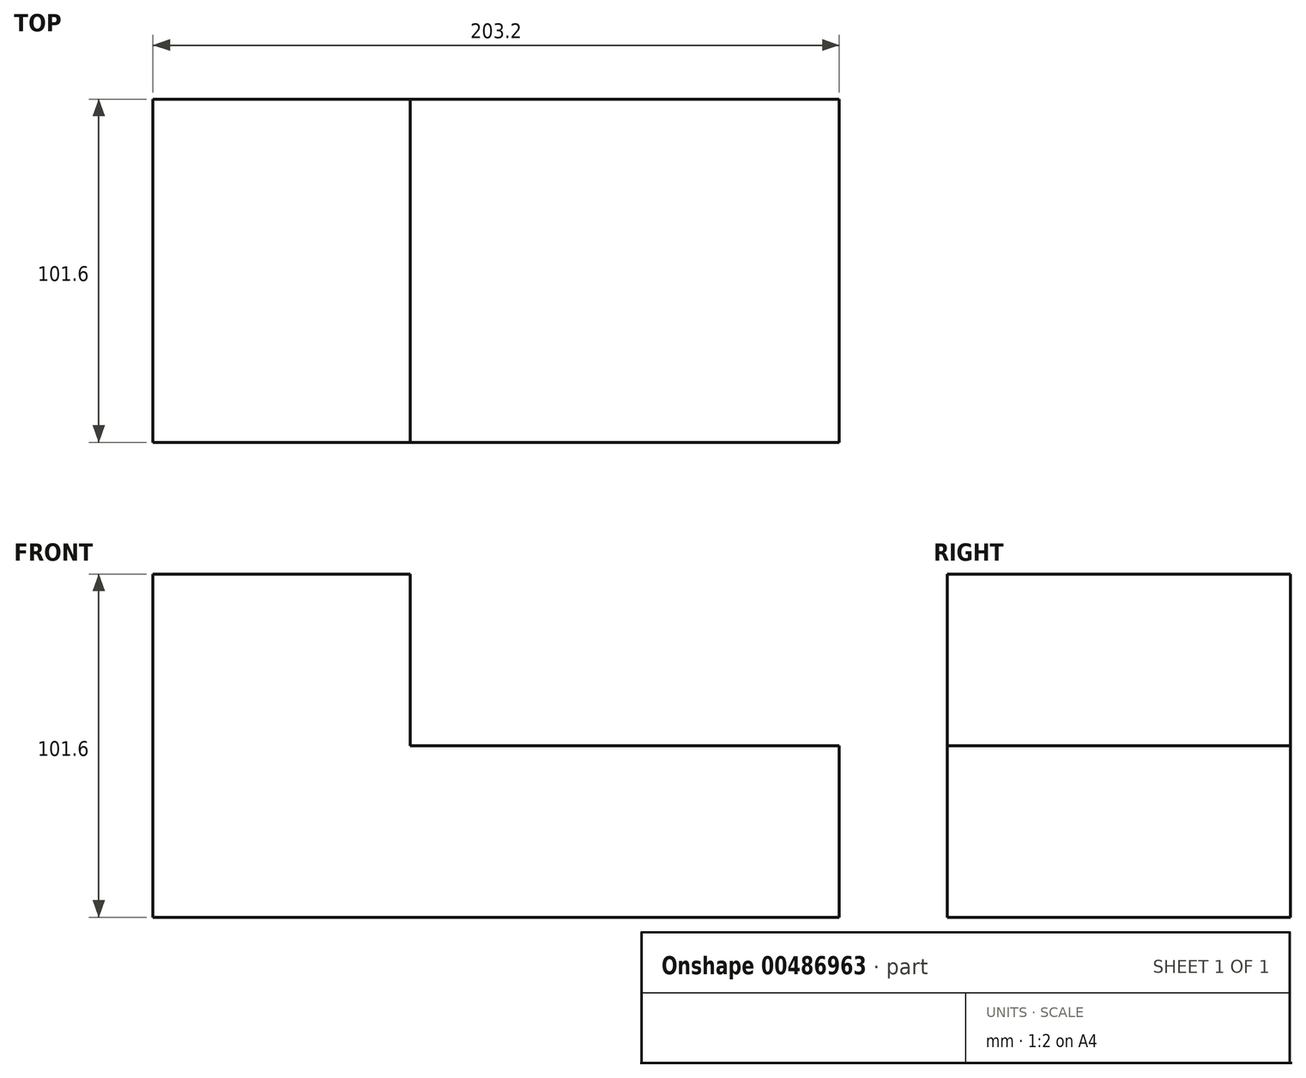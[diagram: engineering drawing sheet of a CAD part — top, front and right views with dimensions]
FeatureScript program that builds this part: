
annotation { "Feature Type Name" : "Feature", "Feature Type Description" : "" }
export const myFeature = defineFeature(function(context is Context, id is Id, definition is map)
    precondition{}
    {
        {
            var Q0;
            Q0=qCreatedBy(makeId("Front.planeOp"),FACE);
            var sketch = newSketch(context, id + "F0", { "sketchPlane" : qUnion([Q0])});
            skLineSegment(sketch, "E0.bottom", {"start": v(0, 0) * mm, "end": v(-203.2, 0) * mm});
            skLineSegment(sketch, "E0.top", {"start": v(-127, 101.6) * mm, "end": v(-203.2, 101.6) * mm});
            skLineSegment(sketch, "E0.left", {"start": v(0, 0) * mm, "end": v(0, 50.8) * mm});
            skLineSegment(sketch, "E0.right", {"start": v(-203.2, 0) * mm, "end": v(-203.2, 101.6) * mm});
            skLineSegment(sketch, "E1.bottom", {"start": v(0, 50.8) * mm, "end": v(-127, 50.8) * mm});
            skLineSegment(sketch, "E1.right", {"start": v(-127, 50.8) * mm, "end": v(-127, 101.6) * mm});
            skSolve(sketch);
        }
        {
            var Q0;
            Q0=makeQuery(id+"F0.imprint","IMPRINT",FACE,{"disambiguationData":[TD([[makeQuery(id+"F0.imprint","IMPRINT",EDGE,{"derivedFrom":sQuery(id+"F0.wireOp",EDGE,"E0.bottom")}),-1.0]])]});
            extrude(context, id + "F1", {"entities" : qUnion([Q0]), "depth" : 101.6 * mm});
        }
    });
